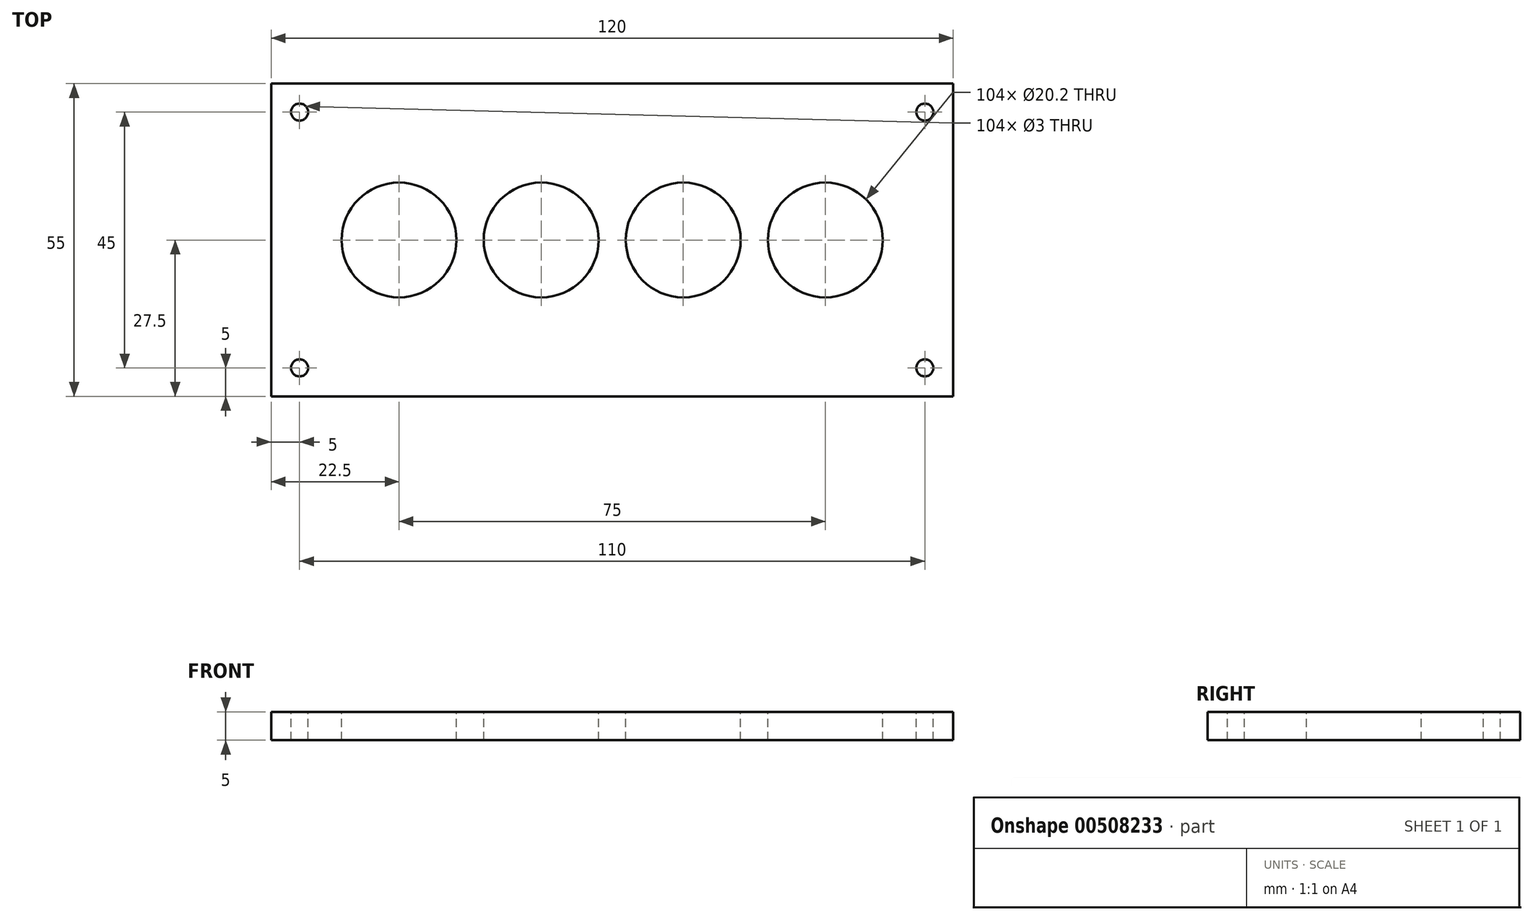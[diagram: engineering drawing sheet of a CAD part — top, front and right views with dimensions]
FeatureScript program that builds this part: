
annotation { "Feature Type Name" : "Feature", "Feature Type Description" : "" }
export const myFeature = defineFeature(function(context is Context, id is Id, definition is map)
    precondition{}
    {
        {
            var Q0;
            Q0=qCreatedBy(makeId("Top.planeOp"),FACE);
            var sketch = newSketch(context, id + "F0", { "sketchPlane" : qUnion([Q0])});
            skLineSegment(sketch, "E0.bottom", {"start": v(0, 0) * mm, "end": v(120, 0) * mm});
            skLineSegment(sketch, "E0.top", {"start": v(0, 55) * mm, "end": v(120, 55) * mm});
            skLineSegment(sketch, "E0.left", {"start": v(0, 0) * mm, "end": v(0, 55) * mm});
            skLineSegment(sketch, "E0.right", {"start": v(120, 0) * mm, "end": v(120, 55) * mm});
            skSolve(sketch);
        }
        {
            var Q0;
            Q0=qSketchRegion(id+"F0",true);
            extrude(context, id + "F1", {"entities" : qUnion([Q0]), "depth" : 5 * mm});
        }
        {
            var Q0;
            Q0=makeQuery(id+"F1.opExtrude","CAP_FACE",FACE,{"disambiguationData":[OSD([sQuery(id+"F0.wireOp",EDGE,"E0.bottom"),sQuery(id+"F0.wireOp",EDGE,"E0.top"),sQuery(id+"F0.wireOp",EDGE,"E0.left"),sQuery(id+"F0.wireOp",EDGE,"E0.right")])],"isStart":false});
            var sketch = newSketch(context, id + "F2", { "sketchPlane" : qUnion([Q0])});
            skCircle(sketch, "E1", {"center": v(22.5, 27.5) * mm, "radius": 10.1 * mm});
            skCircle(sketch, "E2", {"center": v(47.5, 27.5) * mm, "radius": 10.1 * mm});
            skCircle(sketch, "E3", {"center": v(72.5, 27.5) * mm, "radius": 10.1 * mm});
            skCircle(sketch, "E4", {"center": v(97.5, 27.5) * mm, "radius": 10.1 * mm});
            skSolve(sketch);
        }
        {
            var Q0;
            Q0 = qSketchRegion(id + "F2", true);
            extrude(context, id + "F3", {"entities" : qUnion([Q0]), "operationType" : NewBodyOperationType.REMOVE, "endBound" : BoundingType.THROUGH_ALL, "oppositeDirection" : true, "depth" : 25 * mm});
        }
        {
            var Q0;
            Q0=makeQuery(id+"F1.opExtrude","CAP_FACE",FACE,{"disambiguationData":[OSD([sQuery(id+"F0.wireOp",EDGE,"E0.bottom"),sQuery(id+"F0.wireOp",EDGE,"E0.top"),sQuery(id+"F0.wireOp",EDGE,"E0.left"),sQuery(id+"F0.wireOp",EDGE,"E0.right")])],"isStart":false});
            var sketch = newSketch(context, id + "F4", { "sketchPlane" : qUnion([Q0])});
            skLineSegment(sketch, "E5.bottom", {"start": v(5, 50) * mm, "end": v(115, 50) * mm, "construction": true});
            skLineSegment(sketch, "E5.top", {"start": v(5, 5) * mm, "end": v(115, 5) * mm, "construction": true});
            skLineSegment(sketch, "E5.left", {"start": v(5, 50) * mm, "end": v(5, 5) * mm, "construction": true});
            skLineSegment(sketch, "E5.right", {"start": v(115, 50) * mm, "end": v(115, 5) * mm, "construction": true});
            skCircle(sketch, "E6", {"center": v(5, 50) * mm, "radius": 1.5 * mm});
            skCircle(sketch, "E7", {"center": v(115, 50) * mm, "radius": 1.5 * mm});
            skCircle(sketch, "E8", {"center": v(115, 5) * mm, "radius": 1.5 * mm});
            skCircle(sketch, "E9", {"center": v(5, 5) * mm, "radius": 1.5 * mm});
            skSolve(sketch);
        }
        {
            var Q0;
            Q0 = qSketchRegion(id + "F4", true);
            extrude(context, id + "F5", {"entities" : qUnion([Q0]), "operationType" : NewBodyOperationType.REMOVE, "endBound" : BoundingType.THROUGH_ALL, "oppositeDirection" : true, "depth" : 25 * mm});
        }
    });
